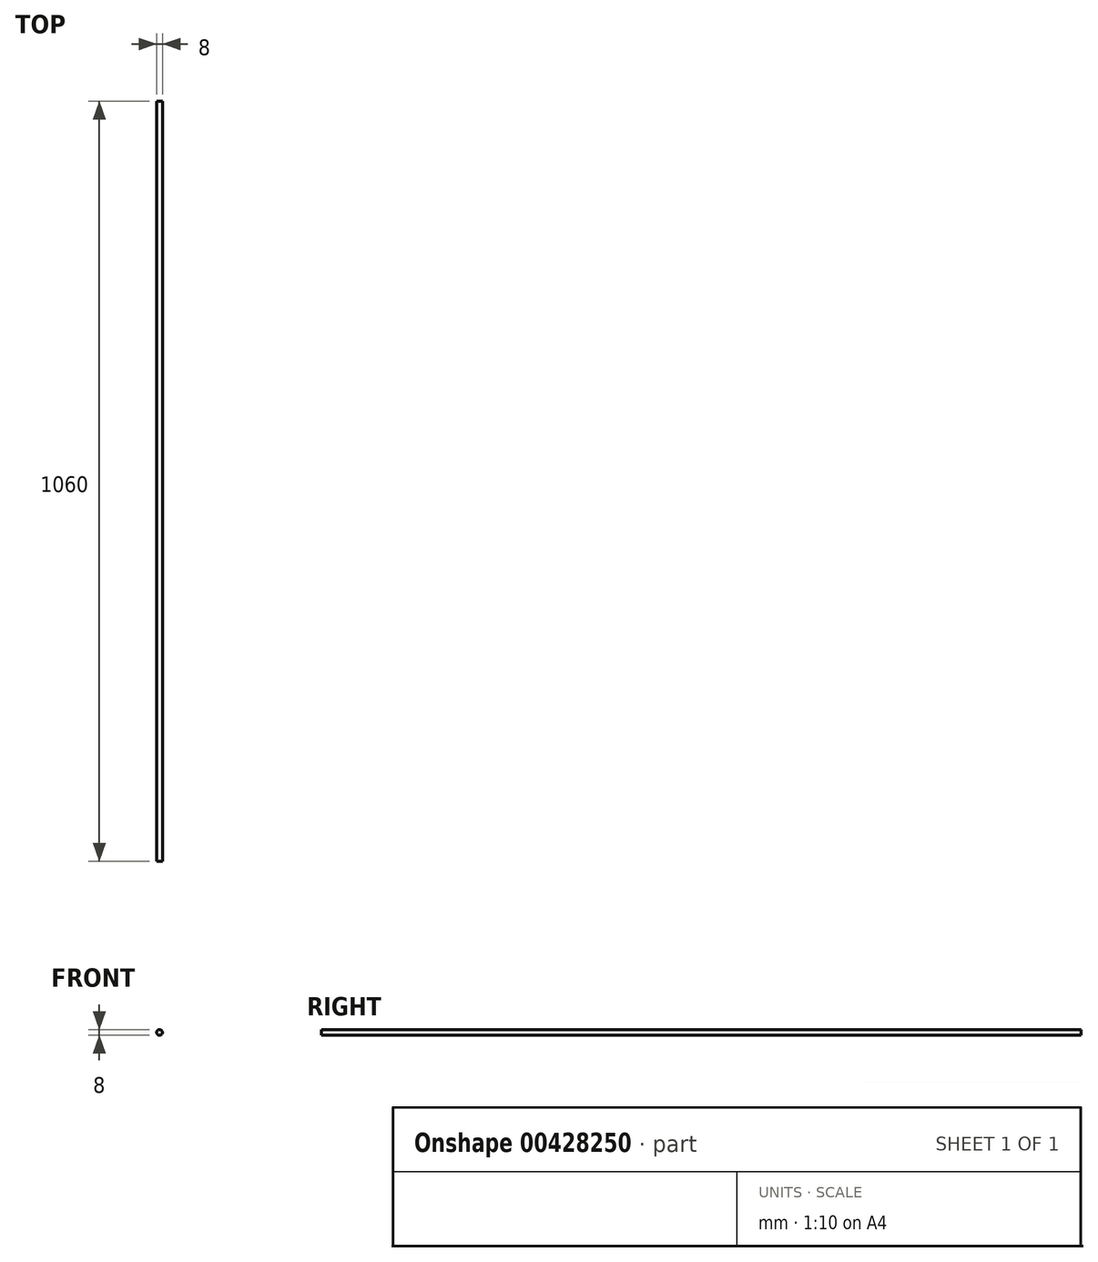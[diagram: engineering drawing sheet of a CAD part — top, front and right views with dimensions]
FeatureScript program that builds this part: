
annotation { "Feature Type Name" : "Feature", "Feature Type Description" : "" }
export const myFeature = defineFeature(function(context is Context, id is Id, definition is map)
    precondition{}
    {
        {
            var Q0;
            Q0=qCreatedBy(makeId("Front.planeOp"),FACE);
            var sketch = newSketch(context, id + "F0", { "sketchPlane" : qUnion([Q0])});
            skCircle(sketch, "E0", {"center": v(0, 0) * mm, "radius": 4 * mm});
            skSolve(sketch);
        }
        {
            var Q0;
            Q0=makeQuery(id+"F0.imprint","IMPRINT",FACE,{"disambiguationData":[TD([[makeQuery(id+"F0.imprint","IMPRINT",EDGE,{"derivedFrom":sQuery(id+"F0.wireOp",EDGE,"E0")}),1.0]])]});
            extrude(context, id + "F1", {"entities" : qUnion([Q0]), "depth" : 1060 * mm, "symmetric" : true});
        }
    });
